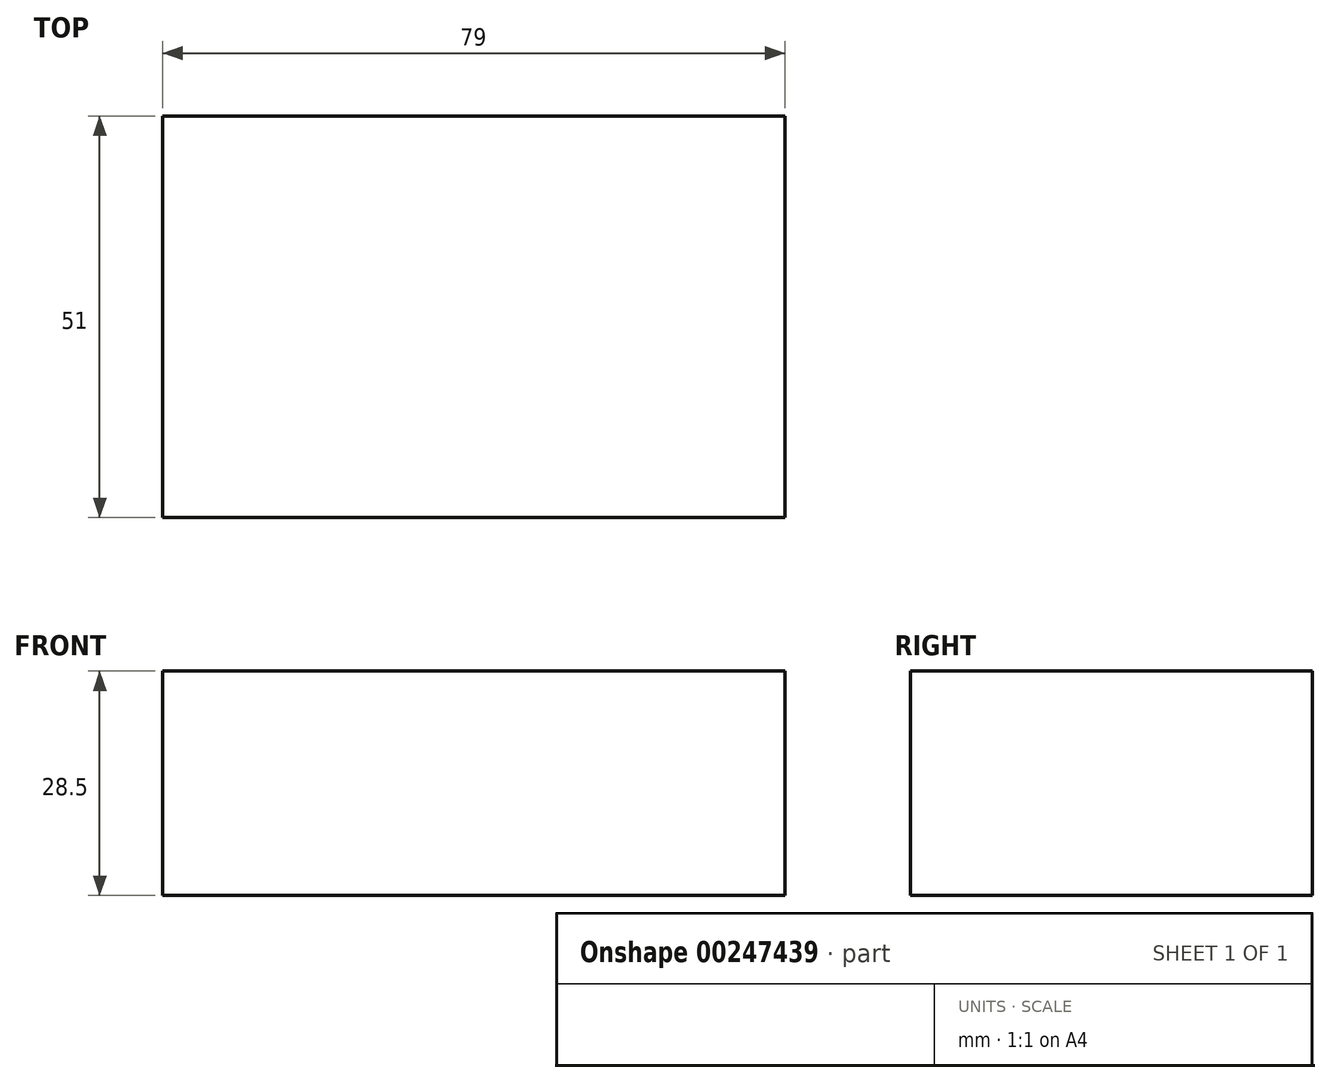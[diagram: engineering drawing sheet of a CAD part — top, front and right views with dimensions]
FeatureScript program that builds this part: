
annotation { "Feature Type Name" : "Feature", "Feature Type Description" : "" }
export const myFeature = defineFeature(function(context is Context, id is Id, definition is map)
    precondition{}
    {
        {
            var Q0;
            Q0=qCreatedBy(makeId("Top.planeOp"),FACE);
            var sketch = newSketch(context, id + "F0", { "sketchPlane" : qUnion([Q0])});
            skLineSegment(sketch, "E0.bottom", {"start": v(0, 0) * mm, "end": v(79, 0) * mm});
            skLineSegment(sketch, "E0.top", {"start": v(0, 51) * mm, "end": v(79, 51) * mm});
            skLineSegment(sketch, "E0.left", {"start": v(0, 0) * mm, "end": v(0, 51) * mm});
            skLineSegment(sketch, "E0.right", {"start": v(79, 0) * mm, "end": v(79, 51) * mm});
            skSolve(sketch);
        }
        {
            var Q0;
            Q0=makeQuery(id+"F0.imprint","IMPRINT",FACE,{"disambiguationData":[TD([[makeQuery(id+"F0.imprint","IMPRINT",EDGE,{"derivedFrom":sQuery(id+"F0.wireOp",EDGE,"E0.bottom")}),1.0]])]});
            extrude(context, id + "F1", {"entities" : qUnion([Q0]), "depth" : 28.5 * mm});
        }
    });
